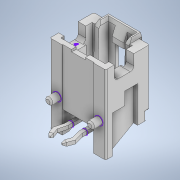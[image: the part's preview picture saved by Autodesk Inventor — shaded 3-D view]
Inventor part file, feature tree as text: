
AUTODESK INVENTOR PART (.ipt)
format: ipt  version: 2022 (Build 260153000, 153)  size: 273,408 bytes
history: native  units: in
note: dims shown in document units (in); Inventor stores cm internally (conversion verified against a paired STEP export)
features: sketch x2, other x1, extrude x1, imported_body x1
ambient origin geometry x8: Origin, YZ Plane, XZ Plane, XY Plane, X Axis, Y Axis, Z Axis, Center Point
bodies: Solid1 (feature_tree)
feature tree (5):
  other  "Repaired Geometry1"
  extrude  "Extrusion1"  [1 undecoded]
  sketch  "3D Sketch1"
  sketch  "Sketch1"  dims[d0=0.0039in d1=0.0in]
  imported_body  "Base1"
note: 1 required parameter value undecoded (feature->parameter linkage not recoverable at this tier; creation-order binding heuristic only, values carry confidence <= 0.55)
